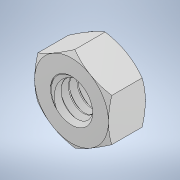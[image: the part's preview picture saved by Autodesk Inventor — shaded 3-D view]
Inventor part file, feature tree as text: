
AUTODESK INVENTOR PART (.ipt)
format: ipt  version: 2022 (Build 260153000, 153)  size: 243,200 bytes
history: mixed  units: in
note: dims shown in document units (in); Inventor stores cm internally (conversion verified against a paired STEP export)
features: mirror x1, imported_body x1
ambient origin geometry x8: Origin, YZ Plane, XZ Plane, XY Plane, X Axis, Y Axis, Z Axis, Center Point
bodies: Solid1 (imported_parasolid)
feature tree (2):
  mirror  "Mirror1"
  imported_body  NMx_Import_Brep_tag  [imported B-rep: ~8 faces, bbox_mm=[2.778125, 4.811854, 0.0]]
